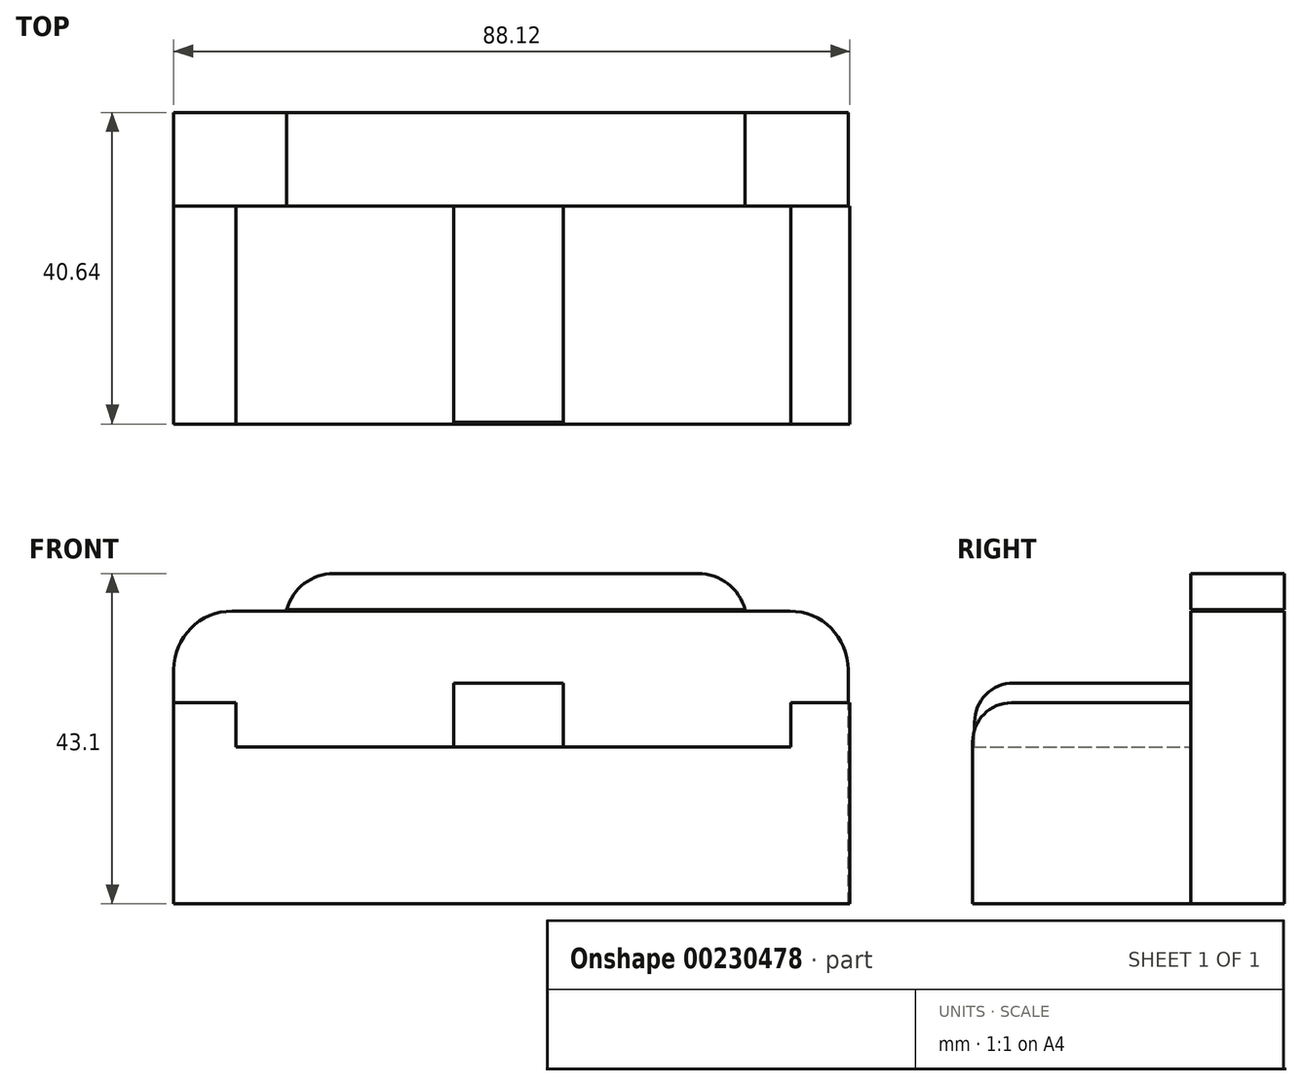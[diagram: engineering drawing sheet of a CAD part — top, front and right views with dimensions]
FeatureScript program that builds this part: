
annotation { "Feature Type Name" : "Feature", "Feature Type Description" : "" }
export const myFeature = defineFeature(function(context is Context, id is Id, definition is map)
    precondition{}
    {
        {
            var Q0;
            Q0=qCreatedBy(makeId("Front.planeOp"),FACE);
            var sketch = newSketch(context, id + "F0", { "sketchPlane" : qUnion([Q0])});
            skLineSegment(sketch, "E0.bottom", {"start": v(-24.75, -36.06) * mm, "end": v(47.58, -36.06) * mm});
            skLineSegment(sketch, "E0.top", {"start": v(-24.75, -56.54) * mm, "end": v(47.58, -56.54) * mm});
            skLineSegment(sketch, "E0.left", {"start": v(-24.75, -36.06) * mm, "end": v(-24.75, -56.54) * mm});
            skLineSegment(sketch, "E0.right", {"start": v(47.58, -36.06) * mm, "end": v(47.58, -56.54) * mm});
            skLineSegment(sketch, "E1.bottom", {"start": v(-24.75, -56.54) * mm, "end": v(-32.86, -56.54) * mm});
            skLineSegment(sketch, "E1.top", {"start": v(-24.75, -30.3) * mm, "end": v(-32.86, -30.3) * mm});
            skLineSegment(sketch, "E1.left", {"start": v(-24.75, -56.54) * mm, "end": v(-24.75, -30.3) * mm});
            skLineSegment(sketch, "E1.right", {"start": v(-32.86, -56.54) * mm, "end": v(-32.86, -30.3) * mm});
            skLineSegment(sketch, "E2.bottom", {"start": v(47.58, -56.54) * mm, "end": v(55.26, -56.54) * mm});
            skLineSegment(sketch, "E2.top", {"start": v(47.58, -30.3) * mm, "end": v(55.26, -30.3) * mm});
            skLineSegment(sketch, "E2.left", {"start": v(47.58, -56.54) * mm, "end": v(47.58, -30.3) * mm});
            skLineSegment(sketch, "E2.right", {"start": v(55.26, -56.54) * mm, "end": v(55.26, -30.3) * mm});
            skSolve(sketch);
        }
        {
            var Q0;
            {var subQ3=sQuery(id+"F0.wireOp",EDGE,"E1.bottom");Q0=makeQuery(id+"F0.imprint","IMPRINT",FACE,{"disambiguationData":[TD([[makeQuery(id+"F0.imprint","IMPRINT",EDGE,{"derivedFrom":subQ3}),-1.0]])]});}
            var Q1;
            {var subQ3=sQuery(id+"F0.wireOp",EDGE,"E2.bottom");Q1=makeQuery(id+"F0.imprint","IMPRINT",FACE,{"disambiguationData":[TD([[makeQuery(id+"F0.imprint","IMPRINT",EDGE,{"derivedFrom":subQ3}),1.0]])]});}
            var Q2;
            {var subQ0=sQuery(id+"F0.wireOp",EDGE,"E0.bottom");Q2=makeQuery(id+"F0.imprint","IMPRINT",FACE,{"disambiguationData":[TD([[makeQuery(id+"F0.imprint","IMPRINT",EDGE,{"derivedFrom":subQ0}),-1.0]])]});}
            extrude(context, id + "F1", {"entities" : qUnion([Q0, Q1, Q2]), "depth" : 28.45 * mm});
        }
        {
            var Q0;
            Q0=qCreatedBy(makeId("Front.planeOp"),FACE);
            var sketch = newSketch(context, id + "F2", { "sketchPlane" : qUnion([Q0])});
            skLineSegment(sketch, "E3.bottom", {"start": v(55.05, -56.54) * mm, "end": v(-32.86, -56.54) * mm});
            skLineSegment(sketch, "E3.top", {"start": v(55.05, -18.35) * mm, "end": v(-32.86, -18.35) * mm});
            skLineSegment(sketch, "E3.left", {"start": v(55.05, -56.54) * mm, "end": v(55.05, -18.35) * mm});
            skLineSegment(sketch, "E3.right", {"start": v(-32.86, -56.54) * mm, "end": v(-32.86, -18.35) * mm});
            skSolve(sketch);
        }
        {
            var Q0;
            Q0=makeQuery(id+"F2.imprint","IMPRINT",FACE,{"disambiguationData":[TD([[makeQuery(id+"F2.imprint","IMPRINT",EDGE,{"derivedFrom":sQuery(id+"F2.wireOp",EDGE,"E3.bottom")}),-1.0]])]});
            extrude(context, id + "F3", {"entities" : qUnion([Q0]), "operationType" : NewBodyOperationType.ADD, "oppositeDirection" : true, "depth" : 12.2 * mm});
        }
        {
            var Q0;
            Q0=qCreatedBy(makeId("Front.planeOp"),FACE);
            var sketch = newSketch(context, id + "F4", { "sketchPlane" : qUnion([Q0])});
            skLineSegment(sketch, "E4.bottom", {"start": v(3.63, -36.06) * mm, "end": v(17.92, -36.06) * mm});
            skLineSegment(sketch, "E4.top", {"start": v(3.63, -27.74) * mm, "end": v(17.92, -27.74) * mm});
            skLineSegment(sketch, "E4.left", {"start": v(3.63, -36.06) * mm, "end": v(3.63, -27.74) * mm});
            skLineSegment(sketch, "E4.right", {"start": v(17.92, -36.06) * mm, "end": v(17.92, -27.74) * mm});
            skSolve(sketch);
        }
        {
            var Q0;
            Q0=makeQuery(id+"F4.imprint","IMPRINT",FACE,{"disambiguationData":[TD([[makeQuery(id+"F4.imprint","IMPRINT",EDGE,{"derivedFrom":sQuery(id+"F4.wireOp",EDGE,"E4.bottom")}),1.0]])]});
            extrude(context, id + "F5", {"entities" : qUnion([Q0]), "operationType" : NewBodyOperationType.ADD, "depth" : 28.2 * mm});
        }
        {
            var Q0;
            Q0=makeQuery(id+"F5.opExtrude","CAP_EDGE",EDGE,{"disambiguationData":[OSD([sQuery(id+"F4.wireOp",EDGE,"E4.top")])],"isStart":false});
            fillet(context, id + "F6", {"entities" : qUnion([Q0]), "radius" : 5.08 * mm, "tangentPropagation" : true, "allowEdgeOverflow" : false});
        }
        {
            var Q0;
            Q0=makeQuery(id+"F1.opExtrude","CAP_EDGE",EDGE,{"disambiguationData":[OSD([sQuery(id+"F0.wireOp",EDGE,"E2.top")])],"isStart":false});
            var Q1;
            Q1=makeQuery(id+"F1.opExtrude","CAP_EDGE",EDGE,{"disambiguationData":[OSD([sQuery(id+"F0.wireOp",EDGE,"E1.top")])],"isStart":false});
            fillet(context, id + "F7", {"entities" : qUnion([Q0, Q1]), "radius" : 5.08 * mm, "tangentPropagation" : true, "allowEdgeOverflow" : false});
        }
        {
            var Q0;
            Q0=makeQuery(id+"F3.opExtrude","SWEPT_EDGE",EDGE,{"disambiguationData":[OSD([sQuery(id+"F2.wireOp",EDGE,"E3.top"),sQuery(id+"F2.wireOp",EDGE,"E3.left")])]});
            fillet(context, id + "F8", {"entities" : qUnion([Q0]), "radius" : 7.62 * mm, "tangentPropagation" : true, "allowEdgeOverflow" : false});
        }
        {
            var Q0;
            Q0=makeQuery(id+"F3.opExtrude","SWEPT_EDGE",EDGE,{"disambiguationData":[OSD([sQuery(id+"F2.wireOp",EDGE,"E3.top"),sQuery(id+"F2.wireOp",EDGE,"E3.right")])]});
            fillet(context, id + "F9", {"entities" : qUnion([Q0]), "radius" : 7.62 * mm, "tangentPropagation" : true, "allowEdgeOverflow" : false});
        }
        {
            var Q0;
            Q0=qCreatedBy(makeId("Front.planeOp"),FACE);
            var sketch = newSketch(context, id + "F10", { "sketchPlane" : qUnion([Q0])});
            skLineSegment(sketch, "E5.bottom", {"start": v(-18.14, -18.14) * mm, "end": v(41.6, -18.14) * mm});
            skLineSegment(sketch, "E5.top", {"start": v(-18.14, -13.44) * mm, "end": v(41.6, -13.44) * mm});
            skLineSegment(sketch, "E5.left", {"start": v(-18.14, -18.14) * mm, "end": v(-18.14, -13.44) * mm});
            skLineSegment(sketch, "E5.right", {"start": v(41.6, -18.14) * mm, "end": v(41.6, -13.44) * mm});
            skSolve(sketch);
        }
        {
            var Q0;
            Q0=makeQuery(id+"F10.imprint","IMPRINT",FACE,{"disambiguationData":[TD([[makeQuery(id+"F10.imprint","IMPRINT",EDGE,{"derivedFrom":sQuery(id+"F10.wireOp",EDGE,"E5.bottom")}),1.0]])]});
            extrude(context, id + "F11", {"entities" : qUnion([Q0]), "oppositeDirection" : true, "depth" : 12.2 * mm});
        }
        {
            var Q0;
            Q0=makeQuery(id+"F11.opExtrude","SWEPT_EDGE",EDGE,{"disambiguationData":[OSD([sQuery(id+"F10.wireOp",EDGE,"E5.top"),sQuery(id+"F10.wireOp",EDGE,"E5.right")])]});
            fillet(context, id + "F12", {"entities" : qUnion([Q0]), "radius" : 6.35 * mm, "tangentPropagation" : true, "allowEdgeOverflow" : false});
        }
        {
            var Q0;
            Q0=makeQuery(id+"F11.opExtrude","SWEPT_EDGE",EDGE,{"disambiguationData":[OSD([sQuery(id+"F10.wireOp",EDGE,"E5.top"),sQuery(id+"F10.wireOp",EDGE,"E5.left")])]});
            fillet(context, id + "F13", {"entities" : qUnion([Q0]), "radius" : 6.35 * mm, "tangentPropagation" : true, "allowEdgeOverflow" : false});
        }
    });
